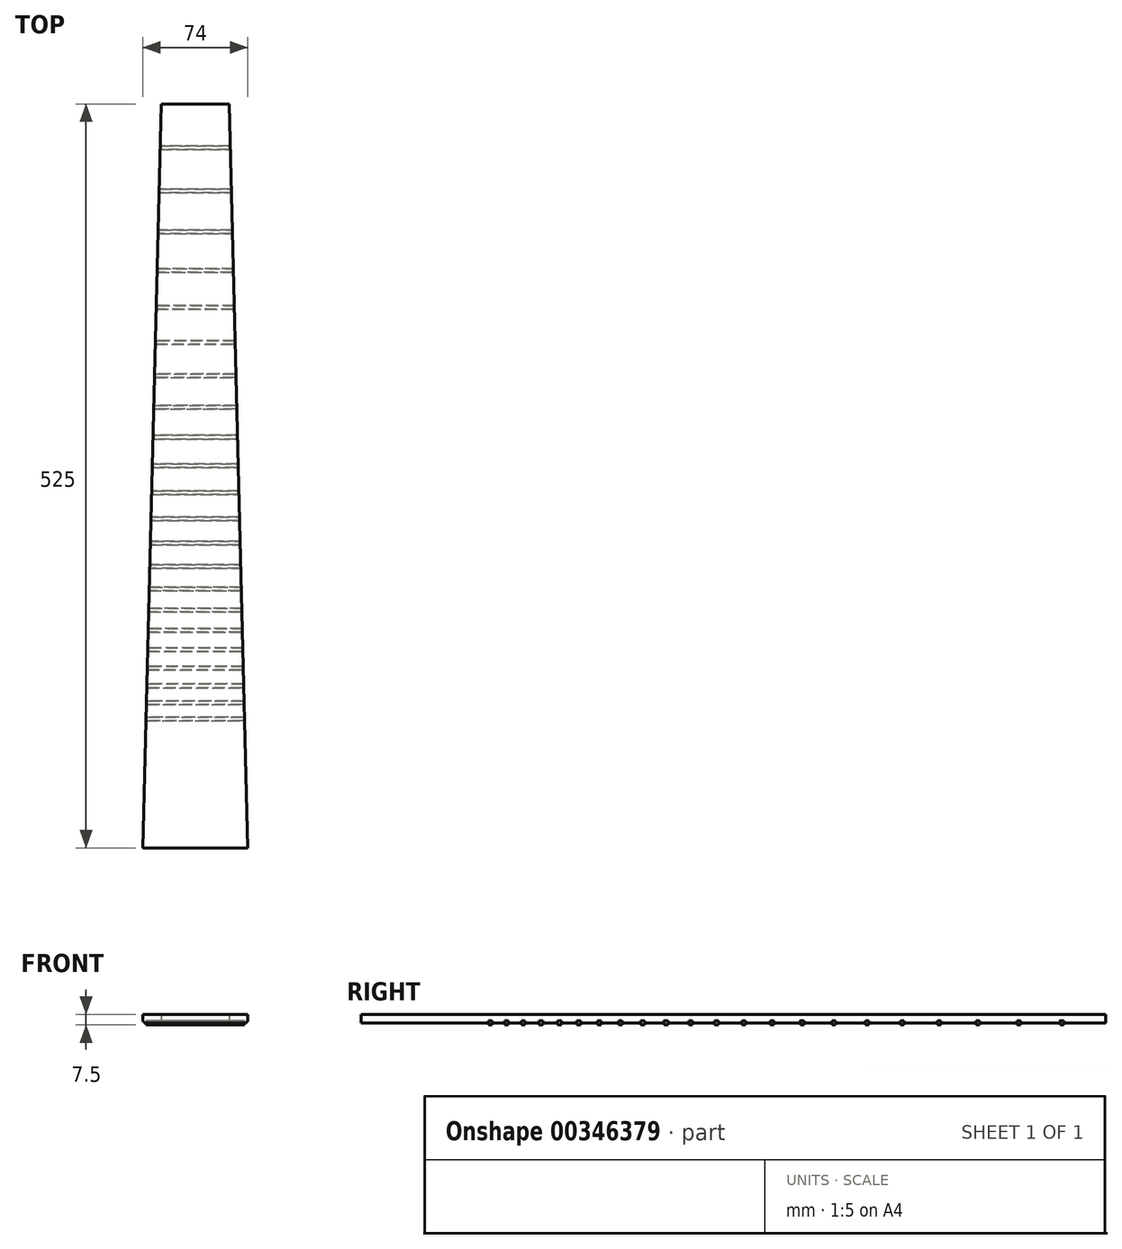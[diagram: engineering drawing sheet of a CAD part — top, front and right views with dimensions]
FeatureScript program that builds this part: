
annotation { "Feature Type Name" : "Feature", "Feature Type Description" : "" }
export const myFeature = defineFeature(function(context is Context, id is Id, definition is map)
    precondition{}
    {
        {
            var Q0;
            Q0=qCreatedBy(makeId("Top.planeOp"),FACE);
            var sketch = newSketch(context, id + "F0", { "sketchPlane" : qUnion([Q0])});
            skLineSegment(sketch, "E0", {"start": v(0, 0) * mm, "end": v(0, 525) * mm, "construction": true});
            skLineSegment(sketch, "E1", {"start": v(0, 525) * mm, "end": v(-24, 525) * mm});
            skLineSegment(sketch, "E2", {"start": v(0, 0) * mm, "end": v(-37, 0) * mm});
            skLineSegment(sketch, "E3", {"start": v(-37, 0) * mm, "end": v(-24, 525) * mm});
            skLineSegment(sketch, "E4", {"start": v(-24.73, 495.53) * mm, "end": v(0, 495.53) * mm});
            skLineSegment(sketch, "E5", {"start": v(-24.8, 492.92) * mm, "end": v(0, 492.92) * mm});
            skLineSegment(sketch, "E6", {"start": v(-25.48, 465.1) * mm, "end": v(0, 465.1) * mm});
            skLineSegment(sketch, "E7", {"start": v(-25.55, 462.49) * mm, "end": v(0, 462.49) * mm});
            skLineSegment(sketch, "E8", {"start": v(-26.2, 436.24) * mm, "end": v(0, 436.24) * mm});
            skLineSegment(sketch, "E9", {"start": v(-26.26, 433.62) * mm, "end": v(0, 433.62) * mm});
            skLineSegment(sketch, "E10", {"start": v(-26.88, 408.84) * mm, "end": v(0, 408.84) * mm});
            skLineSegment(sketch, "E11", {"start": v(-26.94, 406.23) * mm, "end": v(0, 406.23) * mm});
            skLineSegment(sketch, "E12", {"start": v(-27.52, 382.84) * mm, "end": v(0, 382.84) * mm});
            skLineSegment(sketch, "E13", {"start": v(-27.58, 380.22) * mm, "end": v(0, 380.22) * mm});
            skLineSegment(sketch, "E14", {"start": v(-28.13, 358.15) * mm, "end": v(0, 358.15) * mm});
            skLineSegment(sketch, "E15", {"start": v(-28.2, 355.53) * mm, "end": v(0, 355.53) * mm});
            skLineSegment(sketch, "E16", {"start": v(-28.71, 334.7) * mm, "end": v(0, 334.7) * mm});
            skLineSegment(sketch, "E17", {"start": v(-28.78, 332.08) * mm, "end": v(0, 332.08) * mm});
            skLineSegment(sketch, "E18", {"start": v(-29.26, 312.42) * mm, "end": v(0, 312.42) * mm});
            skLineSegment(sketch, "E19", {"start": v(-29.33, 309.8) * mm, "end": v(0, 309.8) * mm});
            skLineSegment(sketch, "E20", {"start": v(-29.79, 291.24) * mm, "end": v(0, 291.24) * mm});
            skLineSegment(sketch, "E21", {"start": v(-29.85, 288.62) * mm, "end": v(0, 288.62) * mm});
            skLineSegment(sketch, "E22", {"start": v(-30.29, 271.1) * mm, "end": v(0, 271.1) * mm});
            skLineSegment(sketch, "E23", {"start": v(-30.35, 268.48) * mm, "end": v(0, 268.48) * mm});
            skLineSegment(sketch, "E24", {"start": v(-30.76, 251.95) * mm, "end": v(0, 251.95) * mm});
            skLineSegment(sketch, "E25", {"start": v(-30.83, 249.33) * mm, "end": v(0, 249.33) * mm});
            skLineSegment(sketch, "E26", {"start": v(-31.21, 233.72) * mm, "end": v(0, 233.72) * mm});
            skLineSegment(sketch, "E27", {"start": v(-31.28, 231.1) * mm, "end": v(0, 231.1) * mm});
            skLineSegment(sketch, "E28", {"start": v(-31.64, 216.37) * mm, "end": v(0, 216.37) * mm});
            skLineSegment(sketch, "E29", {"start": v(-31.7, 213.76) * mm, "end": v(0, 213.76) * mm});
            skLineSegment(sketch, "E30", {"start": v(-32.05, 199.85) * mm, "end": v(0, 199.85) * mm});
            skLineSegment(sketch, "E31", {"start": v(-32.12, 197.23) * mm, "end": v(0, 197.23) * mm});
            skLineSegment(sketch, "E32", {"start": v(-32.44, 184.1) * mm, "end": v(0, 184.1) * mm});
            skLineSegment(sketch, "E33", {"start": v(-32.5, 181.5) * mm, "end": v(0, 181.5) * mm});
            skLineSegment(sketch, "E34", {"start": v(-32.81, 169.1) * mm, "end": v(0, 169.1) * mm});
            skLineSegment(sketch, "E35", {"start": v(-32.88, 166.49) * mm, "end": v(0, 166.49) * mm});
            skLineSegment(sketch, "E36", {"start": v(-33.17, 154.8) * mm, "end": v(0, 154.8) * mm});
            skLineSegment(sketch, "E37", {"start": v(-33.23, 152.18) * mm, "end": v(0, 152.18) * mm});
            skLineSegment(sketch, "E38", {"start": v(-33.5, 141.14) * mm, "end": v(0, 141.14) * mm});
            skLineSegment(sketch, "E39", {"start": v(-33.57, 138.53) * mm, "end": v(0, 138.53) * mm});
            skLineSegment(sketch, "E40", {"start": v(-33.83, 128.1) * mm, "end": v(0, 128.1) * mm});
            skLineSegment(sketch, "E41", {"start": v(-33.9, 125.5) * mm, "end": v(0, 125.5) * mm});
            skLineSegment(sketch, "E42", {"start": v(-34.14, 115.66) * mm, "end": v(0, 115.66) * mm});
            skLineSegment(sketch, "E43", {"start": v(-34.2, 113.04) * mm, "end": v(0, 113.04) * mm});
            skLineSegment(sketch, "E44", {"start": v(-34.43, 103.76) * mm, "end": v(0, 103.76) * mm});
            skLineSegment(sketch, "E45", {"start": v(-34.5, 101.14) * mm, "end": v(0, 101.14) * mm});
            skLineSegment(sketch, "E46", {"start": v(-34.71, 92.38) * mm, "end": v(0, 92.38) * mm});
            skLineSegment(sketch, "E47", {"start": v(-34.78, 89.77) * mm, "end": v(0, 89.77) * mm});
            skLineSegment(sketch, "E48.MirrorCS", {"start": v(0, 525) * mm, "end": v(24, 525) * mm});
            skLineSegment(sketch, "E49.MirrorCS", {"start": v(37, 0) * mm, "end": v(24, 525) * mm});
            skLineSegment(sketch, "E50.MirrorCS", {"start": v(24.73, 495.53) * mm, "end": v(0, 495.53) * mm});
            skLineSegment(sketch, "E51.MirrorCS", {"start": v(24.8, 492.92) * mm, "end": v(0, 492.92) * mm});
            skLineSegment(sketch, "E52.MirrorCS", {"start": v(25.48, 465.1) * mm, "end": v(0, 465.1) * mm});
            skLineSegment(sketch, "E53.MirrorCS", {"start": v(25.55, 462.49) * mm, "end": v(0, 462.49) * mm});
            skLineSegment(sketch, "E54.MirrorCS", {"start": v(26.2, 436.24) * mm, "end": v(0, 436.24) * mm});
            skLineSegment(sketch, "E55.MirrorCS", {"start": v(26.26, 433.62) * mm, "end": v(0, 433.62) * mm});
            skLineSegment(sketch, "E56.MirrorCS", {"start": v(26.88, 408.84) * mm, "end": v(0, 408.84) * mm});
            skLineSegment(sketch, "E57.MirrorCS", {"start": v(26.94, 406.23) * mm, "end": v(0, 406.23) * mm});
            skLineSegment(sketch, "E58.MirrorCS", {"start": v(27.52, 382.84) * mm, "end": v(0, 382.84) * mm});
            skLineSegment(sketch, "E59.MirrorCS", {"start": v(27.58, 380.22) * mm, "end": v(0, 380.22) * mm});
            skLineSegment(sketch, "E60.MirrorCS", {"start": v(28.13, 358.15) * mm, "end": v(0, 358.15) * mm});
            skLineSegment(sketch, "E61.MirrorCS", {"start": v(28.2, 355.53) * mm, "end": v(0, 355.53) * mm});
            skLineSegment(sketch, "E62.MirrorCS", {"start": v(28.71, 334.7) * mm, "end": v(0, 334.7) * mm});
            skLineSegment(sketch, "E63.MirrorCS", {"start": v(28.78, 332.08) * mm, "end": v(0, 332.08) * mm});
            skLineSegment(sketch, "E64.MirrorCS", {"start": v(29.26, 312.42) * mm, "end": v(0, 312.42) * mm});
            skLineSegment(sketch, "E65.MirrorCS", {"start": v(29.33, 309.8) * mm, "end": v(0, 309.8) * mm});
            skLineSegment(sketch, "E66.MirrorCS", {"start": v(29.79, 291.24) * mm, "end": v(0, 291.24) * mm});
            skLineSegment(sketch, "E67.MirrorCS", {"start": v(29.85, 288.62) * mm, "end": v(0, 288.62) * mm});
            skLineSegment(sketch, "E68.MirrorCS", {"start": v(30.29, 271.1) * mm, "end": v(0, 271.1) * mm});
            skLineSegment(sketch, "E69.MirrorCS", {"start": v(30.35, 268.48) * mm, "end": v(0, 268.48) * mm});
            skLineSegment(sketch, "E70.MirrorCS", {"start": v(30.76, 251.95) * mm, "end": v(0, 251.95) * mm});
            skLineSegment(sketch, "E71.MirrorCS", {"start": v(30.83, 249.33) * mm, "end": v(0, 249.33) * mm});
            skLineSegment(sketch, "E72.MirrorCS", {"start": v(31.21, 233.72) * mm, "end": v(0, 233.72) * mm});
            skLineSegment(sketch, "E73.MirrorCS", {"start": v(31.28, 231.1) * mm, "end": v(0, 231.1) * mm});
            skLineSegment(sketch, "E74.MirrorCS", {"start": v(31.64, 216.37) * mm, "end": v(0, 216.37) * mm});
            skLineSegment(sketch, "E75.MirrorCS", {"start": v(31.7, 213.76) * mm, "end": v(0, 213.76) * mm});
            skLineSegment(sketch, "E76.MirrorCS", {"start": v(32.05, 199.85) * mm, "end": v(0, 199.85) * mm});
            skLineSegment(sketch, "E77.MirrorCS", {"start": v(32.12, 197.23) * mm, "end": v(0, 197.23) * mm});
            skLineSegment(sketch, "E78.MirrorCS", {"start": v(32.44, 184.1) * mm, "end": v(0, 184.1) * mm});
            skLineSegment(sketch, "E79.MirrorCS", {"start": v(32.5, 181.5) * mm, "end": v(0, 181.5) * mm});
            skLineSegment(sketch, "E80.MirrorCS", {"start": v(32.81, 169.1) * mm, "end": v(0, 169.1) * mm});
            skLineSegment(sketch, "E81.MirrorCS", {"start": v(32.88, 166.49) * mm, "end": v(0, 166.49) * mm});
            skLineSegment(sketch, "E82.MirrorCS", {"start": v(33.17, 154.8) * mm, "end": v(0, 154.8) * mm});
            skLineSegment(sketch, "E83.MirrorCS", {"start": v(33.23, 152.18) * mm, "end": v(0, 152.18) * mm});
            skLineSegment(sketch, "E84.MirrorCS", {"start": v(33.5, 141.14) * mm, "end": v(0, 141.14) * mm});
            skLineSegment(sketch, "E85.MirrorCS", {"start": v(33.57, 138.53) * mm, "end": v(0, 138.53) * mm});
            skLineSegment(sketch, "E86.MirrorCS", {"start": v(33.83, 128.1) * mm, "end": v(0, 128.1) * mm});
            skLineSegment(sketch, "E87.MirrorCS", {"start": v(33.9, 125.5) * mm, "end": v(0, 125.5) * mm});
            skLineSegment(sketch, "E88.MirrorCS", {"start": v(34.14, 115.66) * mm, "end": v(0, 115.66) * mm});
            skLineSegment(sketch, "E89.MirrorCS", {"start": v(34.2, 113.04) * mm, "end": v(0, 113.04) * mm});
            skLineSegment(sketch, "E90.MirrorCS", {"start": v(34.43, 103.76) * mm, "end": v(0, 103.76) * mm});
            skLineSegment(sketch, "E91.MirrorCS", {"start": v(34.5, 101.14) * mm, "end": v(0, 101.14) * mm});
            skLineSegment(sketch, "E92.MirrorCS", {"start": v(0, 0) * mm, "end": v(37, 0) * mm});
            skLineSegment(sketch, "E93.MirrorCS", {"start": v(34.71, 92.38) * mm, "end": v(0, 92.38) * mm});
            skLineSegment(sketch, "E94.MirrorCS", {"start": v(34.78, 89.77) * mm, "end": v(0, 89.77) * mm});
            skSolve(sketch);
        }
        {
            var Q0;
            Q0 = qSketchRegion(id + "F0", true);
            extrude(context, id + "F1", {"entities" : qUnion([Q0]), "depth" : 6 * mm});
        }
        {
            var Q0;
            {var subQ1=sQuery(id+"F0.wireOp",EDGE,"E4");Q0=makeQuery(id+"F0.imprint","IMPRINT",FACE,{"disambiguationData":[TD([[makeQuery(id+"F0.imprint","IMPRINT",EDGE,{"derivedFrom":subQ1}),-1.0]])]});}
            var Q1;
            {var subQ1=sQuery(id+"F0.wireOp",EDGE,"E6");Q1=makeQuery(id+"F0.imprint","IMPRINT",FACE,{"disambiguationData":[TD([[makeQuery(id+"F0.imprint","IMPRINT",EDGE,{"derivedFrom":subQ1}),-1.0]])]});}
            var Q2;
            {var subQ1=sQuery(id+"F0.wireOp",EDGE,"E8");Q2=makeQuery(id+"F0.imprint","IMPRINT",FACE,{"disambiguationData":[TD([[makeQuery(id+"F0.imprint","IMPRINT",EDGE,{"derivedFrom":subQ1}),-1.0]])]});}
            var Q3;
            {var subQ0=sQuery(id+"F0.wireOp",EDGE,"E10");Q3=makeQuery(id+"F0.imprint","IMPRINT",FACE,{"disambiguationData":[TD([[makeQuery(id+"F0.imprint","IMPRINT",EDGE,{"derivedFrom":subQ0}),-1.0]])]});}
            var Q4;
            {var subQ1=sQuery(id+"F0.wireOp",EDGE,"E12");Q4=makeQuery(id+"F0.imprint","IMPRINT",FACE,{"disambiguationData":[TD([[makeQuery(id+"F0.imprint","IMPRINT",EDGE,{"derivedFrom":subQ1}),-1.0]])]});}
            var Q5;
            {var subQ1=sQuery(id+"F0.wireOp",EDGE,"E14");Q5=makeQuery(id+"F0.imprint","IMPRINT",FACE,{"disambiguationData":[TD([[makeQuery(id+"F0.imprint","IMPRINT",EDGE,{"derivedFrom":subQ1}),-1.0]])]});}
            var Q6;
            {var subQ1=sQuery(id+"F0.wireOp",EDGE,"E16");Q6=makeQuery(id+"F0.imprint","IMPRINT",FACE,{"disambiguationData":[TD([[makeQuery(id+"F0.imprint","IMPRINT",EDGE,{"derivedFrom":subQ1}),-1.0]])]});}
            var Q7;
            {var subQ4=sQuery(id+"F0.wireOp",EDGE,"E18");Q7=makeQuery(id+"F0.imprint","IMPRINT",FACE,{"disambiguationData":[TD([[makeQuery(id+"F0.imprint","IMPRINT",EDGE,{"derivedFrom":subQ4}),-1.0]])]});}
            var Q8;
            {var subQ0=sQuery(id+"F0.wireOp",EDGE,"E20");Q8=makeQuery(id+"F0.imprint","IMPRINT",FACE,{"disambiguationData":[TD([[makeQuery(id+"F0.imprint","IMPRINT",EDGE,{"derivedFrom":subQ0}),-1.0]])]});}
            var Q9;
            {var subQ1=sQuery(id+"F0.wireOp",EDGE,"E22");Q9=makeQuery(id+"F0.imprint","IMPRINT",FACE,{"disambiguationData":[TD([[makeQuery(id+"F0.imprint","IMPRINT",EDGE,{"derivedFrom":subQ1}),-1.0]])]});}
            var Q10;
            {var subQ1=sQuery(id+"F0.wireOp",EDGE,"E24");Q10=makeQuery(id+"F0.imprint","IMPRINT",FACE,{"disambiguationData":[TD([[makeQuery(id+"F0.imprint","IMPRINT",EDGE,{"derivedFrom":subQ1}),-1.0]])]});}
            var Q11;
            {var subQ1=sQuery(id+"F0.wireOp",EDGE,"E26");Q11=makeQuery(id+"F0.imprint","IMPRINT",FACE,{"disambiguationData":[TD([[makeQuery(id+"F0.imprint","IMPRINT",EDGE,{"derivedFrom":subQ1}),-1.0]])]});}
            var Q12;
            {var subQ4=sQuery(id+"F0.wireOp",EDGE,"E28");Q12=makeQuery(id+"F0.imprint","IMPRINT",FACE,{"disambiguationData":[TD([[makeQuery(id+"F0.imprint","IMPRINT",EDGE,{"derivedFrom":subQ4}),-1.0]])]});}
            var Q13;
            {var subQ0=sQuery(id+"F0.wireOp",EDGE,"E30");Q13=makeQuery(id+"F0.imprint","IMPRINT",FACE,{"disambiguationData":[TD([[makeQuery(id+"F0.imprint","IMPRINT",EDGE,{"derivedFrom":subQ0}),-1.0]])]});}
            var Q14;
            {var subQ1=sQuery(id+"F0.wireOp",EDGE,"E32");Q14=makeQuery(id+"F0.imprint","IMPRINT",FACE,{"disambiguationData":[TD([[makeQuery(id+"F0.imprint","IMPRINT",EDGE,{"derivedFrom":subQ1}),-1.0]])]});}
            var Q15;
            {var subQ1=sQuery(id+"F0.wireOp",EDGE,"E34");Q15=makeQuery(id+"F0.imprint","IMPRINT",FACE,{"disambiguationData":[TD([[makeQuery(id+"F0.imprint","IMPRINT",EDGE,{"derivedFrom":subQ1}),-1.0]])]});}
            var Q16;
            {var subQ1=sQuery(id+"F0.wireOp",EDGE,"E36");Q16=makeQuery(id+"F0.imprint","IMPRINT",FACE,{"disambiguationData":[TD([[makeQuery(id+"F0.imprint","IMPRINT",EDGE,{"derivedFrom":subQ1}),-1.0]])]});}
            var Q17;
            {var subQ4=sQuery(id+"F0.wireOp",EDGE,"E38");Q17=makeQuery(id+"F0.imprint","IMPRINT",FACE,{"disambiguationData":[TD([[makeQuery(id+"F0.imprint","IMPRINT",EDGE,{"derivedFrom":subQ4}),-1.0]])]});}
            var Q18;
            {var subQ0=sQuery(id+"F0.wireOp",EDGE,"E40");Q18=makeQuery(id+"F0.imprint","IMPRINT",FACE,{"disambiguationData":[TD([[makeQuery(id+"F0.imprint","IMPRINT",EDGE,{"derivedFrom":subQ0}),-1.0]])]});}
            var Q19;
            {var subQ1=sQuery(id+"F0.wireOp",EDGE,"E46");Q19=makeQuery(id+"F0.imprint","IMPRINT",FACE,{"disambiguationData":[TD([[makeQuery(id+"F0.imprint","IMPRINT",EDGE,{"derivedFrom":subQ1}),-1.0]])]});}
            var Q20;
            {var subQ1=sQuery(id+"F0.wireOp",EDGE,"E44");Q20=makeQuery(id+"F0.imprint","IMPRINT",FACE,{"disambiguationData":[TD([[makeQuery(id+"F0.imprint","IMPRINT",EDGE,{"derivedFrom":subQ1}),-1.0]])]});}
            var Q21;
            {var subQ4=sQuery(id+"F0.wireOp",EDGE,"E42");Q21=makeQuery(id+"F0.imprint","IMPRINT",FACE,{"disambiguationData":[TD([[makeQuery(id+"F0.imprint","IMPRINT",EDGE,{"derivedFrom":subQ4}),-1.0]])]});}
            extrude(context, id + "F2", {"entities" : qUnion([Q0, Q1, Q2, Q3, Q4, Q5, Q6, Q7, Q8, Q9, Q10, Q11, Q12, Q13, Q14, Q15, Q16, Q17, Q18, Q19, Q20, Q21]), "endBound" : BoundingType.SYMMETRIC, "depth" : 3 * mm});
        }
        {
            var Q0;
            Q0=makeQuery(id+"F1.opExtrude","CAP_EDGE",EDGE,{"disambiguationData":[OSD([sQuery(id+"F0.wireOp",EDGE,"E3")])],"isStart":true});
            var Q1;
            Q1=makeQuery(id+"F1.opExtrude","CAP_EDGE",EDGE,{"disambiguationData":[OSD([sQuery(id+"F0.wireOp",EDGE,"E49.MirrorCS")])],"isStart":true});
            fillet(context, id + "F3", {"entities" : qUnion([Q0, Q1]), "radius" : 2 * mm, "tangentPropagation" : true, "allowEdgeOverflow" : false});
        }
        {
            var Q0;
            Q0=makeQuery(id+"F2.opExtrude","SWEPT_BODY",BODY,{"disambiguationData":[OSD([sQuery(id+"F0.wireOp",EDGE,"E3"),sQuery(id+"F0.wireOp",EDGE,"E46"),sQuery(id+"F0.wireOp",EDGE,"E47"),sQuery(id+"F0.wireOp",EDGE,"E49.MirrorCS"),sQuery(id+"F0.wireOp",EDGE,"E93.MirrorCS"),sQuery(id+"F0.wireOp",EDGE,"E94.MirrorCS")])]});
            var Q1;
            Q1=makeQuery(id+"F2.opExtrude","SWEPT_BODY",BODY,{"disambiguationData":[OSD([sQuery(id+"F0.wireOp",EDGE,"E3"),sQuery(id+"F0.wireOp",EDGE,"E44"),sQuery(id+"F0.wireOp",EDGE,"E45"),sQuery(id+"F0.wireOp",EDGE,"E49.MirrorCS"),sQuery(id+"F0.wireOp",EDGE,"E90.MirrorCS"),sQuery(id+"F0.wireOp",EDGE,"E91.MirrorCS")])]});
            var Q2;
            Q2=makeQuery(id+"F2.opExtrude","SWEPT_BODY",BODY,{"disambiguationData":[OSD([sQuery(id+"F0.wireOp",EDGE,"E3"),sQuery(id+"F0.wireOp",EDGE,"E42"),sQuery(id+"F0.wireOp",EDGE,"E43"),sQuery(id+"F0.wireOp",EDGE,"E49.MirrorCS"),sQuery(id+"F0.wireOp",EDGE,"E88.MirrorCS"),sQuery(id+"F0.wireOp",EDGE,"E89.MirrorCS")])]});
            var Q3;
            Q3=makeQuery(id+"F2.opExtrude","SWEPT_BODY",BODY,{"disambiguationData":[OSD([sQuery(id+"F0.wireOp",EDGE,"E3"),sQuery(id+"F0.wireOp",EDGE,"E40"),sQuery(id+"F0.wireOp",EDGE,"E41"),sQuery(id+"F0.wireOp",EDGE,"E49.MirrorCS"),sQuery(id+"F0.wireOp",EDGE,"E86.MirrorCS"),sQuery(id+"F0.wireOp",EDGE,"E87.MirrorCS")])]});
            var Q4;
            Q4=makeQuery(id+"F2.opExtrude","SWEPT_BODY",BODY,{"disambiguationData":[OSD([sQuery(id+"F0.wireOp",EDGE,"E3"),sQuery(id+"F0.wireOp",EDGE,"E38"),sQuery(id+"F0.wireOp",EDGE,"E39"),sQuery(id+"F0.wireOp",EDGE,"E49.MirrorCS"),sQuery(id+"F0.wireOp",EDGE,"E84.MirrorCS"),sQuery(id+"F0.wireOp",EDGE,"E85.MirrorCS")])]});
            var Q5;
            Q5=makeQuery(id+"F2.opExtrude","SWEPT_BODY",BODY,{"disambiguationData":[OSD([sQuery(id+"F0.wireOp",EDGE,"E3"),sQuery(id+"F0.wireOp",EDGE,"E36"),sQuery(id+"F0.wireOp",EDGE,"E37"),sQuery(id+"F0.wireOp",EDGE,"E49.MirrorCS"),sQuery(id+"F0.wireOp",EDGE,"E82.MirrorCS"),sQuery(id+"F0.wireOp",EDGE,"E83.MirrorCS")])]});
            var Q6;
            Q6=makeQuery(id+"F2.opExtrude","SWEPT_BODY",BODY,{"disambiguationData":[OSD([sQuery(id+"F0.wireOp",EDGE,"E3"),sQuery(id+"F0.wireOp",EDGE,"E34"),sQuery(id+"F0.wireOp",EDGE,"E35"),sQuery(id+"F0.wireOp",EDGE,"E49.MirrorCS"),sQuery(id+"F0.wireOp",EDGE,"E80.MirrorCS"),sQuery(id+"F0.wireOp",EDGE,"E81.MirrorCS")])]});
            var Q7;
            Q7=makeQuery(id+"F2.opExtrude","SWEPT_BODY",BODY,{"disambiguationData":[OSD([sQuery(id+"F0.wireOp",EDGE,"E3"),sQuery(id+"F0.wireOp",EDGE,"E32"),sQuery(id+"F0.wireOp",EDGE,"E33"),sQuery(id+"F0.wireOp",EDGE,"E49.MirrorCS"),sQuery(id+"F0.wireOp",EDGE,"E78.MirrorCS"),sQuery(id+"F0.wireOp",EDGE,"E79.MirrorCS")])]});
            var Q8;
            Q8=makeQuery(id+"F2.opExtrude","SWEPT_BODY",BODY,{"disambiguationData":[OSD([sQuery(id+"F0.wireOp",EDGE,"E3"),sQuery(id+"F0.wireOp",EDGE,"E30"),sQuery(id+"F0.wireOp",EDGE,"E31"),sQuery(id+"F0.wireOp",EDGE,"E49.MirrorCS"),sQuery(id+"F0.wireOp",EDGE,"E76.MirrorCS"),sQuery(id+"F0.wireOp",EDGE,"E77.MirrorCS")])]});
            var Q9;
            Q9=makeQuery(id+"F2.opExtrude","SWEPT_BODY",BODY,{"disambiguationData":[OSD([sQuery(id+"F0.wireOp",EDGE,"E3"),sQuery(id+"F0.wireOp",EDGE,"E28"),sQuery(id+"F0.wireOp",EDGE,"E29"),sQuery(id+"F0.wireOp",EDGE,"E49.MirrorCS"),sQuery(id+"F0.wireOp",EDGE,"E74.MirrorCS"),sQuery(id+"F0.wireOp",EDGE,"E75.MirrorCS")])]});
            var Q10;
            Q10=makeQuery(id+"F2.opExtrude","SWEPT_BODY",BODY,{"disambiguationData":[OSD([sQuery(id+"F0.wireOp",EDGE,"E3"),sQuery(id+"F0.wireOp",EDGE,"E26"),sQuery(id+"F0.wireOp",EDGE,"E27"),sQuery(id+"F0.wireOp",EDGE,"E49.MirrorCS"),sQuery(id+"F0.wireOp",EDGE,"E72.MirrorCS"),sQuery(id+"F0.wireOp",EDGE,"E73.MirrorCS")])]});
            var Q11;
            Q11=makeQuery(id+"F2.opExtrude","SWEPT_BODY",BODY,{"disambiguationData":[OSD([sQuery(id+"F0.wireOp",EDGE,"E3"),sQuery(id+"F0.wireOp",EDGE,"E24"),sQuery(id+"F0.wireOp",EDGE,"E25"),sQuery(id+"F0.wireOp",EDGE,"E49.MirrorCS"),sQuery(id+"F0.wireOp",EDGE,"E70.MirrorCS"),sQuery(id+"F0.wireOp",EDGE,"E71.MirrorCS")])]});
            var Q12;
            Q12=makeQuery(id+"F2.opExtrude","SWEPT_BODY",BODY,{"disambiguationData":[OSD([sQuery(id+"F0.wireOp",EDGE,"E3"),sQuery(id+"F0.wireOp",EDGE,"E22"),sQuery(id+"F0.wireOp",EDGE,"E23"),sQuery(id+"F0.wireOp",EDGE,"E49.MirrorCS"),sQuery(id+"F0.wireOp",EDGE,"E68.MirrorCS"),sQuery(id+"F0.wireOp",EDGE,"E69.MirrorCS")])]});
            var Q13;
            Q13=makeQuery(id+"F2.opExtrude","SWEPT_BODY",BODY,{"disambiguationData":[OSD([sQuery(id+"F0.wireOp",EDGE,"E3"),sQuery(id+"F0.wireOp",EDGE,"E20"),sQuery(id+"F0.wireOp",EDGE,"E21"),sQuery(id+"F0.wireOp",EDGE,"E49.MirrorCS"),sQuery(id+"F0.wireOp",EDGE,"E66.MirrorCS"),sQuery(id+"F0.wireOp",EDGE,"E67.MirrorCS")])]});
            var Q14;
            Q14=makeQuery(id+"F2.opExtrude","SWEPT_BODY",BODY,{"disambiguationData":[OSD([sQuery(id+"F0.wireOp",EDGE,"E3"),sQuery(id+"F0.wireOp",EDGE,"E18"),sQuery(id+"F0.wireOp",EDGE,"E19"),sQuery(id+"F0.wireOp",EDGE,"E49.MirrorCS"),sQuery(id+"F0.wireOp",EDGE,"E64.MirrorCS"),sQuery(id+"F0.wireOp",EDGE,"E65.MirrorCS")])]});
            var Q15;
            Q15=makeQuery(id+"F2.opExtrude","SWEPT_BODY",BODY,{"disambiguationData":[OSD([sQuery(id+"F0.wireOp",EDGE,"E3"),sQuery(id+"F0.wireOp",EDGE,"E16"),sQuery(id+"F0.wireOp",EDGE,"E17"),sQuery(id+"F0.wireOp",EDGE,"E49.MirrorCS"),sQuery(id+"F0.wireOp",EDGE,"E62.MirrorCS"),sQuery(id+"F0.wireOp",EDGE,"E63.MirrorCS")])]});
            var Q16;
            Q16=makeQuery(id+"F2.opExtrude","SWEPT_BODY",BODY,{"disambiguationData":[OSD([sQuery(id+"F0.wireOp",EDGE,"E3"),sQuery(id+"F0.wireOp",EDGE,"E14"),sQuery(id+"F0.wireOp",EDGE,"E15"),sQuery(id+"F0.wireOp",EDGE,"E49.MirrorCS"),sQuery(id+"F0.wireOp",EDGE,"E60.MirrorCS"),sQuery(id+"F0.wireOp",EDGE,"E61.MirrorCS")])]});
            var Q17;
            Q17=makeQuery(id+"F2.opExtrude","SWEPT_BODY",BODY,{"disambiguationData":[OSD([sQuery(id+"F0.wireOp",EDGE,"E3"),sQuery(id+"F0.wireOp",EDGE,"E12"),sQuery(id+"F0.wireOp",EDGE,"E13"),sQuery(id+"F0.wireOp",EDGE,"E49.MirrorCS"),sQuery(id+"F0.wireOp",EDGE,"E58.MirrorCS"),sQuery(id+"F0.wireOp",EDGE,"E59.MirrorCS")])]});
            var Q18;
            Q18=makeQuery(id+"F2.opExtrude","SWEPT_BODY",BODY,{"disambiguationData":[OSD([sQuery(id+"F0.wireOp",EDGE,"E3"),sQuery(id+"F0.wireOp",EDGE,"E10"),sQuery(id+"F0.wireOp",EDGE,"E11"),sQuery(id+"F0.wireOp",EDGE,"E49.MirrorCS"),sQuery(id+"F0.wireOp",EDGE,"E56.MirrorCS"),sQuery(id+"F0.wireOp",EDGE,"E57.MirrorCS")])]});
            var Q19;
            Q19=makeQuery(id+"F2.opExtrude","SWEPT_BODY",BODY,{"disambiguationData":[OSD([sQuery(id+"F0.wireOp",EDGE,"E3"),sQuery(id+"F0.wireOp",EDGE,"E8"),sQuery(id+"F0.wireOp",EDGE,"E9"),sQuery(id+"F0.wireOp",EDGE,"E49.MirrorCS"),sQuery(id+"F0.wireOp",EDGE,"E54.MirrorCS"),sQuery(id+"F0.wireOp",EDGE,"E55.MirrorCS")])]});
            var Q20;
            Q20=makeQuery(id+"F2.opExtrude","SWEPT_BODY",BODY,{"disambiguationData":[OSD([sQuery(id+"F0.wireOp",EDGE,"E3"),sQuery(id+"F0.wireOp",EDGE,"E6"),sQuery(id+"F0.wireOp",EDGE,"E7"),sQuery(id+"F0.wireOp",EDGE,"E49.MirrorCS"),sQuery(id+"F0.wireOp",EDGE,"E52.MirrorCS"),sQuery(id+"F0.wireOp",EDGE,"E53.MirrorCS")])]});
            var Q21;
            Q21=makeQuery(id+"F2.opExtrude","SWEPT_BODY",BODY,{"disambiguationData":[OSD([sQuery(id+"F0.wireOp",EDGE,"E3"),sQuery(id+"F0.wireOp",EDGE,"E4"),sQuery(id+"F0.wireOp",EDGE,"E5"),sQuery(id+"F0.wireOp",EDGE,"E49.MirrorCS"),sQuery(id+"F0.wireOp",EDGE,"E50.MirrorCS"),sQuery(id+"F0.wireOp",EDGE,"E51.MirrorCS")])]});
            var Q22;
            Q22=makeQuery(id+"F1.opExtrude","SWEPT_BODY",BODY,{"disambiguationData":[OSD([sQuery(id+"F0.wireOp",EDGE,"E1"),sQuery(id+"F0.wireOp",EDGE,"E2"),sQuery(id+"F0.wireOp",EDGE,"E3"),sQuery(id+"F0.wireOp",EDGE,"E48.MirrorCS"),sQuery(id+"F0.wireOp",EDGE,"E49.MirrorCS"),sQuery(id+"F0.wireOp",EDGE,"E92.MirrorCS")])]});
            booleanBodies(context, id + "F4", {"operationType" : BooleanOperationType.SUBTRACTION, "tools" : qUnion([Q0, Q1, Q2, Q3, Q4, Q5, Q6, Q7, Q8, Q9, Q10, Q11, Q12, Q13, Q14, Q15, Q16, Q17, Q18, Q19, Q20, Q21]), "targets" : qUnion([Q22]), "keepTools" : true});
        }
        {
            var Q0;
            {var subQ0=sQuery(id+"F0.wireOp",EDGE,"E3");Q0=makeQuery(id+"F2.opExtrude","CAP_EDGE",EDGE,{"disambiguationData":[OSD([subQ0]),TDD([makeQuery(id+"F0.imprint","IMPRINT",EDGE,{"disambiguationData":[TD([[makeQuery(id+"F0.imprint","INTERSECT",VERTEX,{"derivedFrom":[subQ0,sQuery(id+"F0.wireOp",EDGE,"E4")]}),1.0]])],"derivedFrom":subQ0})])],"isStart":false});}
            var Q1;
            {var subQ0=sQuery(id+"F0.wireOp",EDGE,"E49.MirrorCS");Q1=makeQuery(id+"F2.opExtrude","CAP_EDGE",EDGE,{"disambiguationData":[OSD([subQ0]),TDD([makeQuery(id+"F0.imprint","IMPRINT",EDGE,{"disambiguationData":[TD([[makeQuery(id+"F0.imprint","INTERSECT",VERTEX,{"derivedFrom":[subQ0,sQuery(id+"F0.wireOp",EDGE,"E50.MirrorCS")]}),1.0]])],"derivedFrom":subQ0})])],"isStart":false});}
            var Q2;
            {var subQ0=sQuery(id+"F0.wireOp",EDGE,"E49.MirrorCS");Q2=makeQuery(id+"F2.opExtrude","CAP_EDGE",EDGE,{"disambiguationData":[OSD([subQ0]),TDD([makeQuery(id+"F0.imprint","IMPRINT",EDGE,{"disambiguationData":[TD([[makeQuery(id+"F0.imprint","INTERSECT",VERTEX,{"derivedFrom":[subQ0,sQuery(id+"F0.wireOp",EDGE,"E52.MirrorCS")]}),1.0]])],"derivedFrom":subQ0})])],"isStart":false});}
            var Q3;
            {var subQ0=sQuery(id+"F0.wireOp",EDGE,"E3");Q3=makeQuery(id+"F2.opExtrude","CAP_EDGE",EDGE,{"disambiguationData":[OSD([subQ0]),TDD([makeQuery(id+"F0.imprint","IMPRINT",EDGE,{"disambiguationData":[TD([[makeQuery(id+"F0.imprint","INTERSECT",VERTEX,{"derivedFrom":[subQ0,sQuery(id+"F0.wireOp",EDGE,"E6")]}),1.0]])],"derivedFrom":subQ0})])],"isStart":false});}
            var Q4;
            {var subQ0=sQuery(id+"F0.wireOp",EDGE,"E3");Q4=makeQuery(id+"F2.opExtrude","CAP_EDGE",EDGE,{"disambiguationData":[OSD([subQ0]),TDD([makeQuery(id+"F0.imprint","IMPRINT",EDGE,{"disambiguationData":[TD([[makeQuery(id+"F0.imprint","INTERSECT",VERTEX,{"derivedFrom":[subQ0,sQuery(id+"F0.wireOp",EDGE,"E8")]}),1.0]])],"derivedFrom":subQ0})])],"isStart":false});}
            var Q5;
            {var subQ0=sQuery(id+"F0.wireOp",EDGE,"E49.MirrorCS");Q5=makeQuery(id+"F2.opExtrude","CAP_EDGE",EDGE,{"disambiguationData":[OSD([subQ0]),TDD([makeQuery(id+"F0.imprint","IMPRINT",EDGE,{"disambiguationData":[TD([[makeQuery(id+"F0.imprint","INTERSECT",VERTEX,{"derivedFrom":[subQ0,sQuery(id+"F0.wireOp",EDGE,"E54.MirrorCS")]}),1.0]])],"derivedFrom":subQ0})])],"isStart":false});}
            var Q6;
            {var subQ0=sQuery(id+"F0.wireOp",EDGE,"E3");Q6=makeQuery(id+"F2.opExtrude","CAP_EDGE",EDGE,{"disambiguationData":[OSD([subQ0]),TDD([makeQuery(id+"F0.imprint","IMPRINT",EDGE,{"disambiguationData":[TD([[makeQuery(id+"F0.imprint","INTERSECT",VERTEX,{"derivedFrom":[subQ0,sQuery(id+"F0.wireOp",EDGE,"E10")]}),1.0]])],"derivedFrom":subQ0})])],"isStart":false});}
            var Q7;
            {var subQ0=sQuery(id+"F0.wireOp",EDGE,"E49.MirrorCS");Q7=makeQuery(id+"F2.opExtrude","CAP_EDGE",EDGE,{"disambiguationData":[OSD([subQ0]),TDD([makeQuery(id+"F0.imprint","IMPRINT",EDGE,{"disambiguationData":[TD([[makeQuery(id+"F0.imprint","INTERSECT",VERTEX,{"derivedFrom":[subQ0,sQuery(id+"F0.wireOp",EDGE,"E56.MirrorCS")]}),1.0]])],"derivedFrom":subQ0})])],"isStart":false});}
            var Q8;
            {var subQ0=sQuery(id+"F0.wireOp",EDGE,"E49.MirrorCS");Q8=makeQuery(id+"F2.opExtrude","CAP_EDGE",EDGE,{"disambiguationData":[OSD([subQ0]),TDD([makeQuery(id+"F0.imprint","IMPRINT",EDGE,{"disambiguationData":[TD([[makeQuery(id+"F0.imprint","INTERSECT",VERTEX,{"derivedFrom":[subQ0,sQuery(id+"F0.wireOp",EDGE,"E58.MirrorCS")]}),1.0]])],"derivedFrom":subQ0})])],"isStart":false});}
            var Q9;
            {var subQ0=sQuery(id+"F0.wireOp",EDGE,"E3");Q9=makeQuery(id+"F2.opExtrude","CAP_EDGE",EDGE,{"disambiguationData":[OSD([subQ0]),TDD([makeQuery(id+"F0.imprint","IMPRINT",EDGE,{"disambiguationData":[TD([[makeQuery(id+"F0.imprint","INTERSECT",VERTEX,{"derivedFrom":[subQ0,sQuery(id+"F0.wireOp",EDGE,"E12")]}),1.0]])],"derivedFrom":subQ0})])],"isStart":false});}
            var Q10;
            {var subQ0=sQuery(id+"F0.wireOp",EDGE,"E3");Q10=makeQuery(id+"F2.opExtrude","CAP_EDGE",EDGE,{"disambiguationData":[OSD([subQ0]),TDD([makeQuery(id+"F0.imprint","IMPRINT",EDGE,{"disambiguationData":[TD([[makeQuery(id+"F0.imprint","INTERSECT",VERTEX,{"derivedFrom":[subQ0,sQuery(id+"F0.wireOp",EDGE,"E14")]}),1.0]])],"derivedFrom":subQ0})])],"isStart":false});}
            var Q11;
            {var subQ0=sQuery(id+"F0.wireOp",EDGE,"E49.MirrorCS");Q11=makeQuery(id+"F2.opExtrude","CAP_EDGE",EDGE,{"disambiguationData":[OSD([subQ0]),TDD([makeQuery(id+"F0.imprint","IMPRINT",EDGE,{"disambiguationData":[TD([[makeQuery(id+"F0.imprint","INTERSECT",VERTEX,{"derivedFrom":[subQ0,sQuery(id+"F0.wireOp",EDGE,"E60.MirrorCS")]}),1.0]])],"derivedFrom":subQ0})])],"isStart":false});}
            var Q12;
            {var subQ0=sQuery(id+"F0.wireOp",EDGE,"E49.MirrorCS");Q12=makeQuery(id+"F2.opExtrude","CAP_EDGE",EDGE,{"disambiguationData":[OSD([subQ0]),TDD([makeQuery(id+"F0.imprint","IMPRINT",EDGE,{"disambiguationData":[TD([[makeQuery(id+"F0.imprint","INTERSECT",VERTEX,{"derivedFrom":[subQ0,sQuery(id+"F0.wireOp",EDGE,"E62.MirrorCS")]}),1.0]])],"derivedFrom":subQ0})])],"isStart":false});}
            var Q13;
            {var subQ0=sQuery(id+"F0.wireOp",EDGE,"E3");Q13=makeQuery(id+"F2.opExtrude","CAP_EDGE",EDGE,{"disambiguationData":[OSD([subQ0]),TDD([makeQuery(id+"F0.imprint","IMPRINT",EDGE,{"disambiguationData":[TD([[makeQuery(id+"F0.imprint","INTERSECT",VERTEX,{"derivedFrom":[subQ0,sQuery(id+"F0.wireOp",EDGE,"E16")]}),1.0]])],"derivedFrom":subQ0})])],"isStart":false});}
            var Q14;
            {var subQ0=sQuery(id+"F0.wireOp",EDGE,"E3");Q14=makeQuery(id+"F2.opExtrude","CAP_EDGE",EDGE,{"disambiguationData":[OSD([subQ0]),TDD([makeQuery(id+"F0.imprint","IMPRINT",EDGE,{"disambiguationData":[TD([[makeQuery(id+"F0.imprint","INTERSECT",VERTEX,{"derivedFrom":[subQ0,sQuery(id+"F0.wireOp",EDGE,"E18")]}),1.0]])],"derivedFrom":subQ0})])],"isStart":false});}
            var Q15;
            {var subQ0=sQuery(id+"F0.wireOp",EDGE,"E49.MirrorCS");Q15=makeQuery(id+"F2.opExtrude","CAP_EDGE",EDGE,{"disambiguationData":[OSD([subQ0]),TDD([makeQuery(id+"F0.imprint","IMPRINT",EDGE,{"disambiguationData":[TD([[makeQuery(id+"F0.imprint","INTERSECT",VERTEX,{"derivedFrom":[subQ0,sQuery(id+"F0.wireOp",EDGE,"E64.MirrorCS")]}),1.0]])],"derivedFrom":subQ0})])],"isStart":false});}
            var Q16;
            {var subQ0=sQuery(id+"F0.wireOp",EDGE,"E49.MirrorCS");Q16=makeQuery(id+"F2.opExtrude","CAP_EDGE",EDGE,{"disambiguationData":[OSD([subQ0]),TDD([makeQuery(id+"F0.imprint","IMPRINT",EDGE,{"disambiguationData":[TD([[makeQuery(id+"F0.imprint","INTERSECT",VERTEX,{"derivedFrom":[subQ0,sQuery(id+"F0.wireOp",EDGE,"E66.MirrorCS")]}),1.0]])],"derivedFrom":subQ0})])],"isStart":false});}
            var Q17;
            {var subQ0=sQuery(id+"F0.wireOp",EDGE,"E3");Q17=makeQuery(id+"F2.opExtrude","CAP_EDGE",EDGE,{"disambiguationData":[OSD([subQ0]),TDD([makeQuery(id+"F0.imprint","IMPRINT",EDGE,{"disambiguationData":[TD([[makeQuery(id+"F0.imprint","INTERSECT",VERTEX,{"derivedFrom":[subQ0,sQuery(id+"F0.wireOp",EDGE,"E20")]}),1.0]])],"derivedFrom":subQ0})])],"isStart":false});}
            var Q18;
            {var subQ0=sQuery(id+"F0.wireOp",EDGE,"E3");Q18=makeQuery(id+"F2.opExtrude","CAP_EDGE",EDGE,{"disambiguationData":[OSD([subQ0]),TDD([makeQuery(id+"F0.imprint","IMPRINT",EDGE,{"disambiguationData":[TD([[makeQuery(id+"F0.imprint","INTERSECT",VERTEX,{"derivedFrom":[subQ0,sQuery(id+"F0.wireOp",EDGE,"E22")]}),1.0]])],"derivedFrom":subQ0})])],"isStart":false});}
            var Q19;
            {var subQ0=sQuery(id+"F0.wireOp",EDGE,"E49.MirrorCS");Q19=makeQuery(id+"F2.opExtrude","CAP_EDGE",EDGE,{"disambiguationData":[OSD([subQ0]),TDD([makeQuery(id+"F0.imprint","IMPRINT",EDGE,{"disambiguationData":[TD([[makeQuery(id+"F0.imprint","INTERSECT",VERTEX,{"derivedFrom":[subQ0,sQuery(id+"F0.wireOp",EDGE,"E68.MirrorCS")]}),1.0]])],"derivedFrom":subQ0})])],"isStart":false});}
            var Q20;
            {var subQ0=sQuery(id+"F0.wireOp",EDGE,"E49.MirrorCS");Q20=makeQuery(id+"F2.opExtrude","CAP_EDGE",EDGE,{"disambiguationData":[OSD([subQ0]),TDD([makeQuery(id+"F0.imprint","IMPRINT",EDGE,{"disambiguationData":[TD([[makeQuery(id+"F0.imprint","INTERSECT",VERTEX,{"derivedFrom":[subQ0,sQuery(id+"F0.wireOp",EDGE,"E70.MirrorCS")]}),1.0]])],"derivedFrom":subQ0})])],"isStart":false});}
            var Q21;
            {var subQ0=sQuery(id+"F0.wireOp",EDGE,"E3");Q21=makeQuery(id+"F2.opExtrude","CAP_EDGE",EDGE,{"disambiguationData":[OSD([subQ0]),TDD([makeQuery(id+"F0.imprint","IMPRINT",EDGE,{"disambiguationData":[TD([[makeQuery(id+"F0.imprint","INTERSECT",VERTEX,{"derivedFrom":[subQ0,sQuery(id+"F0.wireOp",EDGE,"E24")]}),1.0]])],"derivedFrom":subQ0})])],"isStart":false});}
            var Q22;
            {var subQ0=sQuery(id+"F0.wireOp",EDGE,"E3");Q22=makeQuery(id+"F2.opExtrude","CAP_EDGE",EDGE,{"disambiguationData":[OSD([subQ0]),TDD([makeQuery(id+"F0.imprint","IMPRINT",EDGE,{"disambiguationData":[TD([[makeQuery(id+"F0.imprint","INTERSECT",VERTEX,{"derivedFrom":[subQ0,sQuery(id+"F0.wireOp",EDGE,"E26")]}),1.0]])],"derivedFrom":subQ0})])],"isStart":false});}
            var Q23;
            {var subQ0=sQuery(id+"F0.wireOp",EDGE,"E49.MirrorCS");Q23=makeQuery(id+"F2.opExtrude","CAP_EDGE",EDGE,{"disambiguationData":[OSD([subQ0]),TDD([makeQuery(id+"F0.imprint","IMPRINT",EDGE,{"disambiguationData":[TD([[makeQuery(id+"F0.imprint","INTERSECT",VERTEX,{"derivedFrom":[subQ0,sQuery(id+"F0.wireOp",EDGE,"E72.MirrorCS")]}),1.0]])],"derivedFrom":subQ0})])],"isStart":false});}
            var Q24;
            {var subQ0=sQuery(id+"F0.wireOp",EDGE,"E3");Q24=makeQuery(id+"F2.opExtrude","CAP_EDGE",EDGE,{"disambiguationData":[OSD([subQ0]),TDD([makeQuery(id+"F0.imprint","IMPRINT",EDGE,{"disambiguationData":[TD([[makeQuery(id+"F0.imprint","INTERSECT",VERTEX,{"derivedFrom":[subQ0,sQuery(id+"F0.wireOp",EDGE,"E28")]}),1.0]])],"derivedFrom":subQ0})])],"isStart":false});}
            var Q25;
            {var subQ0=sQuery(id+"F0.wireOp",EDGE,"E49.MirrorCS");Q25=makeQuery(id+"F2.opExtrude","CAP_EDGE",EDGE,{"disambiguationData":[OSD([subQ0]),TDD([makeQuery(id+"F0.imprint","IMPRINT",EDGE,{"disambiguationData":[TD([[makeQuery(id+"F0.imprint","INTERSECT",VERTEX,{"derivedFrom":[subQ0,sQuery(id+"F0.wireOp",EDGE,"E74.MirrorCS")]}),1.0]])],"derivedFrom":subQ0})])],"isStart":false});}
            var Q26;
            {var subQ0=sQuery(id+"F0.wireOp",EDGE,"E49.MirrorCS");Q26=makeQuery(id+"F2.opExtrude","CAP_EDGE",EDGE,{"disambiguationData":[OSD([subQ0]),TDD([makeQuery(id+"F0.imprint","IMPRINT",EDGE,{"disambiguationData":[TD([[makeQuery(id+"F0.imprint","INTERSECT",VERTEX,{"derivedFrom":[subQ0,sQuery(id+"F0.wireOp",EDGE,"E76.MirrorCS")]}),1.0]])],"derivedFrom":subQ0})])],"isStart":false});}
            var Q27;
            {var subQ0=sQuery(id+"F0.wireOp",EDGE,"E3");Q27=makeQuery(id+"F2.opExtrude","CAP_EDGE",EDGE,{"disambiguationData":[OSD([subQ0]),TDD([makeQuery(id+"F0.imprint","IMPRINT",EDGE,{"disambiguationData":[TD([[makeQuery(id+"F0.imprint","INTERSECT",VERTEX,{"derivedFrom":[subQ0,sQuery(id+"F0.wireOp",EDGE,"E30")]}),1.0]])],"derivedFrom":subQ0})])],"isStart":false});}
            var Q28;
            {var subQ0=sQuery(id+"F0.wireOp",EDGE,"E3");Q28=makeQuery(id+"F2.opExtrude","CAP_EDGE",EDGE,{"disambiguationData":[OSD([subQ0]),TDD([makeQuery(id+"F0.imprint","IMPRINT",EDGE,{"disambiguationData":[TD([[makeQuery(id+"F0.imprint","INTERSECT",VERTEX,{"derivedFrom":[subQ0,sQuery(id+"F0.wireOp",EDGE,"E32")]}),1.0]])],"derivedFrom":subQ0})])],"isStart":false});}
            var Q29;
            {var subQ0=sQuery(id+"F0.wireOp",EDGE,"E49.MirrorCS");Q29=makeQuery(id+"F2.opExtrude","CAP_EDGE",EDGE,{"disambiguationData":[OSD([subQ0]),TDD([makeQuery(id+"F0.imprint","IMPRINT",EDGE,{"disambiguationData":[TD([[makeQuery(id+"F0.imprint","INTERSECT",VERTEX,{"derivedFrom":[subQ0,sQuery(id+"F0.wireOp",EDGE,"E78.MirrorCS")]}),1.0]])],"derivedFrom":subQ0})])],"isStart":false});}
            var Q30;
            {var subQ0=sQuery(id+"F0.wireOp",EDGE,"E49.MirrorCS");Q30=makeQuery(id+"F2.opExtrude","CAP_EDGE",EDGE,{"disambiguationData":[OSD([subQ0]),TDD([makeQuery(id+"F0.imprint","IMPRINT",EDGE,{"disambiguationData":[TD([[makeQuery(id+"F0.imprint","INTERSECT",VERTEX,{"derivedFrom":[subQ0,sQuery(id+"F0.wireOp",EDGE,"E80.MirrorCS")]}),1.0]])],"derivedFrom":subQ0})])],"isStart":false});}
            var Q31;
            {var subQ0=sQuery(id+"F0.wireOp",EDGE,"E3");Q31=makeQuery(id+"F2.opExtrude","CAP_EDGE",EDGE,{"disambiguationData":[OSD([subQ0]),TDD([makeQuery(id+"F0.imprint","IMPRINT",EDGE,{"disambiguationData":[TD([[makeQuery(id+"F0.imprint","INTERSECT",VERTEX,{"derivedFrom":[subQ0,sQuery(id+"F0.wireOp",EDGE,"E34")]}),1.0]])],"derivedFrom":subQ0})])],"isStart":false});}
            var Q32;
            {var subQ0=sQuery(id+"F0.wireOp",EDGE,"E3");Q32=makeQuery(id+"F2.opExtrude","CAP_EDGE",EDGE,{"disambiguationData":[OSD([subQ0]),TDD([makeQuery(id+"F0.imprint","IMPRINT",EDGE,{"disambiguationData":[TD([[makeQuery(id+"F0.imprint","INTERSECT",VERTEX,{"derivedFrom":[subQ0,sQuery(id+"F0.wireOp",EDGE,"E36")]}),1.0]])],"derivedFrom":subQ0})])],"isStart":false});}
            var Q33;
            {var subQ0=sQuery(id+"F0.wireOp",EDGE,"E49.MirrorCS");Q33=makeQuery(id+"F2.opExtrude","CAP_EDGE",EDGE,{"disambiguationData":[OSD([subQ0]),TDD([makeQuery(id+"F0.imprint","IMPRINT",EDGE,{"disambiguationData":[TD([[makeQuery(id+"F0.imprint","INTERSECT",VERTEX,{"derivedFrom":[subQ0,sQuery(id+"F0.wireOp",EDGE,"E82.MirrorCS")]}),1.0]])],"derivedFrom":subQ0})])],"isStart":false});}
            var Q34;
            {var subQ0=sQuery(id+"F0.wireOp",EDGE,"E49.MirrorCS");Q34=makeQuery(id+"F2.opExtrude","CAP_EDGE",EDGE,{"disambiguationData":[OSD([subQ0]),TDD([makeQuery(id+"F0.imprint","IMPRINT",EDGE,{"disambiguationData":[TD([[makeQuery(id+"F0.imprint","INTERSECT",VERTEX,{"derivedFrom":[subQ0,sQuery(id+"F0.wireOp",EDGE,"E84.MirrorCS")]}),1.0]])],"derivedFrom":subQ0})])],"isStart":false});}
            var Q35;
            {var subQ0=sQuery(id+"F0.wireOp",EDGE,"E3");Q35=makeQuery(id+"F2.opExtrude","CAP_EDGE",EDGE,{"disambiguationData":[OSD([subQ0]),TDD([makeQuery(id+"F0.imprint","IMPRINT",EDGE,{"disambiguationData":[TD([[makeQuery(id+"F0.imprint","INTERSECT",VERTEX,{"derivedFrom":[subQ0,sQuery(id+"F0.wireOp",EDGE,"E38")]}),1.0]])],"derivedFrom":subQ0})])],"isStart":false});}
            var Q36;
            {var subQ0=sQuery(id+"F0.wireOp",EDGE,"E3");Q36=makeQuery(id+"F2.opExtrude","CAP_EDGE",EDGE,{"disambiguationData":[OSD([subQ0]),TDD([makeQuery(id+"F0.imprint","IMPRINT",EDGE,{"disambiguationData":[TD([[makeQuery(id+"F0.imprint","INTERSECT",VERTEX,{"derivedFrom":[subQ0,sQuery(id+"F0.wireOp",EDGE,"E40")]}),1.0]])],"derivedFrom":subQ0})])],"isStart":false});}
            var Q37;
            {var subQ0=sQuery(id+"F0.wireOp",EDGE,"E49.MirrorCS");Q37=makeQuery(id+"F2.opExtrude","CAP_EDGE",EDGE,{"disambiguationData":[OSD([subQ0]),TDD([makeQuery(id+"F0.imprint","IMPRINT",EDGE,{"disambiguationData":[TD([[makeQuery(id+"F0.imprint","INTERSECT",VERTEX,{"derivedFrom":[subQ0,sQuery(id+"F0.wireOp",EDGE,"E86.MirrorCS")]}),1.0]])],"derivedFrom":subQ0})])],"isStart":false});}
            var Q38;
            {var subQ0=sQuery(id+"F0.wireOp",EDGE,"E49.MirrorCS");Q38=makeQuery(id+"F2.opExtrude","CAP_EDGE",EDGE,{"disambiguationData":[OSD([subQ0]),TDD([makeQuery(id+"F0.imprint","IMPRINT",EDGE,{"disambiguationData":[TD([[makeQuery(id+"F0.imprint","INTERSECT",VERTEX,{"derivedFrom":[subQ0,sQuery(id+"F0.wireOp",EDGE,"E88.MirrorCS")]}),1.0]])],"derivedFrom":subQ0})])],"isStart":false});}
            var Q39;
            {var subQ0=sQuery(id+"F0.wireOp",EDGE,"E49.MirrorCS");Q39=makeQuery(id+"F2.opExtrude","CAP_EDGE",EDGE,{"disambiguationData":[OSD([subQ0]),TDD([makeQuery(id+"F0.imprint","IMPRINT",EDGE,{"disambiguationData":[TD([[makeQuery(id+"F0.imprint","INTERSECT",VERTEX,{"derivedFrom":[subQ0,sQuery(id+"F0.wireOp",EDGE,"E90.MirrorCS")]}),1.0]])],"derivedFrom":subQ0})])],"isStart":false});}
            var Q40;
            {var subQ0=sQuery(id+"F0.wireOp",EDGE,"E49.MirrorCS");Q40=makeQuery(id+"F2.opExtrude","CAP_EDGE",EDGE,{"disambiguationData":[OSD([subQ0]),TDD([makeQuery(id+"F0.imprint","IMPRINT",EDGE,{"disambiguationData":[TD([[makeQuery(id+"F0.imprint","INTERSECT",VERTEX,{"derivedFrom":[subQ0,sQuery(id+"F0.wireOp",EDGE,"E93.MirrorCS")]}),1.0]])],"derivedFrom":subQ0})])],"isStart":false});}
            var Q41;
            {var subQ0=sQuery(id+"F0.wireOp",EDGE,"E3");Q41=makeQuery(id+"F2.opExtrude","CAP_EDGE",EDGE,{"disambiguationData":[OSD([subQ0]),TDD([makeQuery(id+"F0.imprint","IMPRINT",EDGE,{"disambiguationData":[TD([[makeQuery(id+"F0.imprint","INTERSECT",VERTEX,{"derivedFrom":[subQ0,sQuery(id+"F0.wireOp",EDGE,"E42")]}),1.0]])],"derivedFrom":subQ0})])],"isStart":false});}
            var Q42;
            {var subQ0=sQuery(id+"F0.wireOp",EDGE,"E3");Q42=makeQuery(id+"F2.opExtrude","CAP_EDGE",EDGE,{"disambiguationData":[OSD([subQ0]),TDD([makeQuery(id+"F0.imprint","IMPRINT",EDGE,{"disambiguationData":[TD([[makeQuery(id+"F0.imprint","INTERSECT",VERTEX,{"derivedFrom":[subQ0,sQuery(id+"F0.wireOp",EDGE,"E46")]}),1.0]])],"derivedFrom":subQ0})])],"isStart":false});}
            var Q43;
            {var subQ0=sQuery(id+"F0.wireOp",EDGE,"E3");Q43=makeQuery(id+"F2.opExtrude","CAP_EDGE",EDGE,{"disambiguationData":[OSD([subQ0]),TDD([makeQuery(id+"F0.imprint","IMPRINT",EDGE,{"disambiguationData":[TD([[makeQuery(id+"F0.imprint","INTERSECT",VERTEX,{"derivedFrom":[subQ0,sQuery(id+"F0.wireOp",EDGE,"E44")]}),1.0]])],"derivedFrom":subQ0})])],"isStart":false});}
            fillet(context, id + "F5", {"entities" : qUnion([Q0, Q1, Q2, Q3, Q4, Q5, Q6, Q7, Q8, Q9, Q10, Q11, Q12, Q13, Q14, Q15, Q16, Q17, Q18, Q19, Q20, Q21, Q22, Q23, Q24, Q25, Q26, Q27, Q28, Q29, Q30, Q31, Q32, Q33, Q34, Q35, Q36, Q37, Q38, Q39, Q40, Q41, Q42, Q43]), "radius" : 1 * mm, "tangentPropagation" : true, "allowEdgeOverflow" : false});
        }
    });
